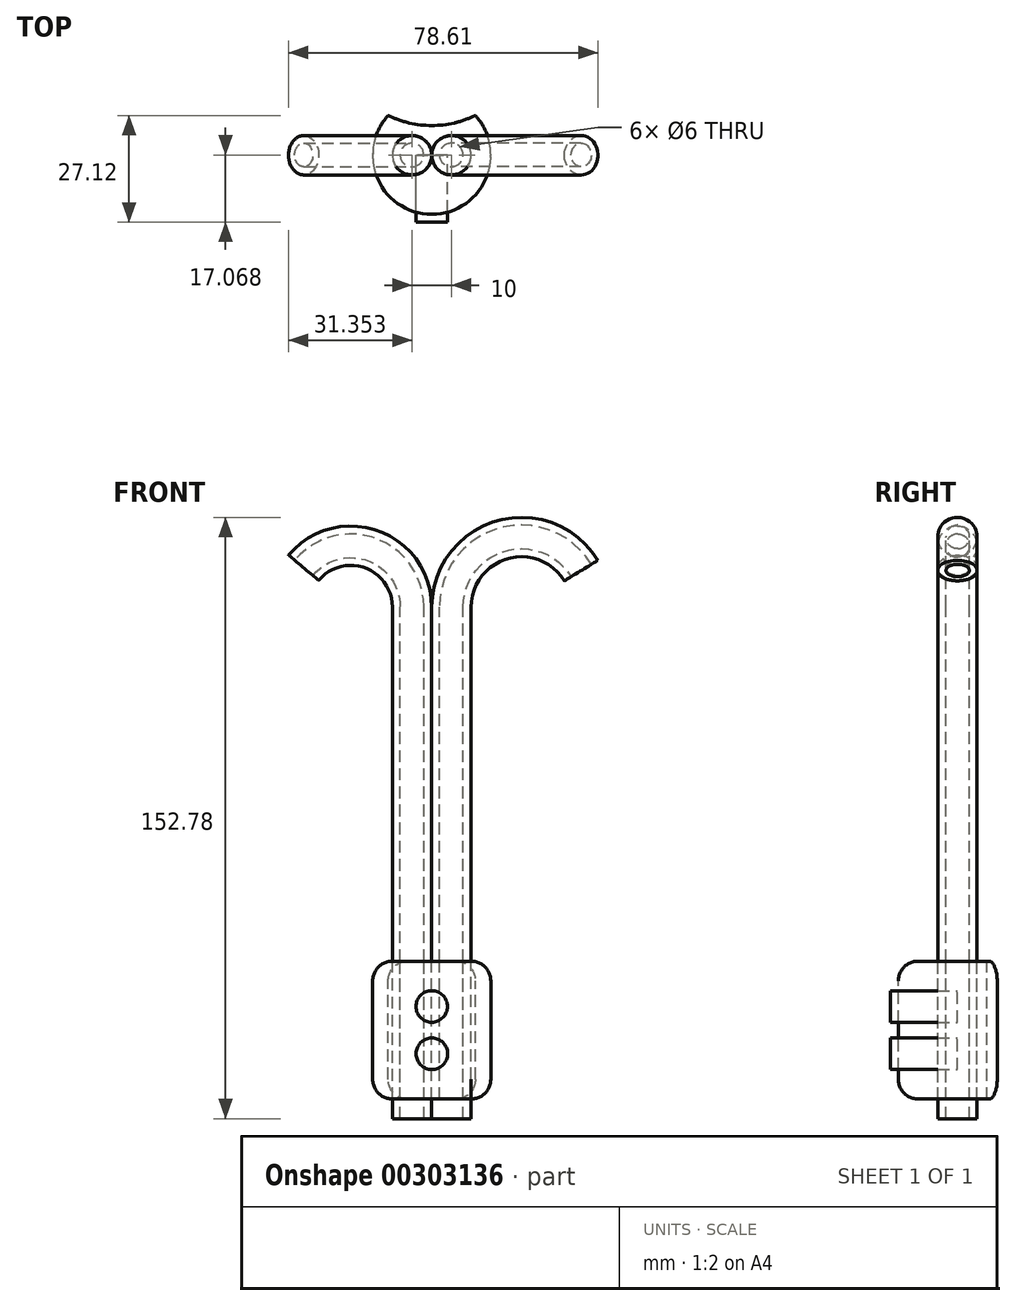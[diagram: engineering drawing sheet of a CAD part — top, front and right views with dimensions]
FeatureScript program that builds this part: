
annotation { "Feature Type Name" : "Feature", "Feature Type Description" : "" }
export const myFeature = defineFeature(function(context is Context, id is Id, definition is map)
    precondition{}
    {
        {
            var Q0;
            Q0=qCreatedBy(makeId("Top.planeOp"),FACE);
            var sketch = newSketch(context, id + "F0", { "sketchPlane" : qUnion([Q0])});
            skCircle(sketch, "E0", {"center": v(0, 0) * mm, "radius": 15 * mm});
            skCircle(sketch, "E1", {"center": v(0, 32.54) * mm, "radius": 25 * mm});
            skCircle(sketch, "E2", {"center": v(-5, 0) * mm, "radius": 5 * mm});
            skCircle(sketch, "E3.1.0.0", {"center": v(5, 0) * mm, "radius": 5 * mm});
            skLineSegment(sketch, "E3.direction1", {"start": v(-5, 0) * mm, "end": v(5, 0) * mm, "construction": true});
            skCircle(sketch, "E4", {"center": v(-5.03, 0.07) * mm, "radius": 3 * mm});
            skCircle(sketch, "E5.1.0.0", {"center": v(4.97, 0.07) * mm, "radius": 3 * mm});
            skLineSegment(sketch, "E5.direction1", {"start": v(-5.03, 0.07) * mm, "end": v(4.97, 0.07) * mm, "construction": true});
            skSolve(sketch);
        }
        {
            var Q0;
            Q0=qCreatedBy(makeId("Front.planeOp"),FACE);
            var sketch = newSketch(context, id + "F1", { "sketchPlane" : qUnion([Q0])});
            skLineSegment(sketch, "E6", {"start": v(-5, 0) * mm, "end": v(-5, 90) * mm});
            skLineSegment(sketch, "E7", {"start": v(5, 0) * mm, "end": v(5, 90) * mm});
            skArc(sketch, "E8", {"start": v(-5, 90) * mm, "mid": v(-15.27, 104.64) * mm, "end": v(-32.54, 99.97) * mm});
            skArc(sketch, "E9", {"start": v(37.96, 99.26) * mm, "mid": v(17.97, 107.12) * mm, "end": v(5, 90) * mm});
            skCircle(sketch, "E10", {"center": v(0, -11.5) * mm, "radius": 4 * mm});
            skCircle(sketch, "E11.0.1.0", {"center": v(0.03, -23.5) * mm, "radius": 4 * mm});
            skLineSegment(sketch, "E11.direction1", {"start": v(0, -11.5) * mm, "end": v(2.66, -11.5) * mm, "construction": true});
            skLineSegment(sketch, "E11.direction2", {"start": v(0, -11.5) * mm, "end": v(0.03, -23.5) * mm, "construction": true});
            skSolve(sketch);
        }
        {
            var Q0;
            Q0=makeQuery(id+"F0.imprint","IMPRINT",FACE,{"disambiguationData":[TD([[makeQuery(id+"F0.imprint","IMPRINT",EDGE,{"derivedFrom":sQuery(id+"F0.wireOp",EDGE,"E2")}),1.0]])]});
            var Q1;
            Q1=sQuery(id+"F1.wireOp",EDGE,"E6");
            var Q2;
            Q2=sQuery(id+"F1.wireOp",EDGE,"E8");
            sweep(context, id + "F2", {"profiles" : qUnion([Q0]), "path" : qUnion([Q1, Q2])});
        }
        {
            var Q0;
            Q0=makeQuery(id+"F0.imprint","IMPRINT",FACE,{"disambiguationData":[TD([[makeQuery(id+"F0.imprint","IMPRINT",EDGE,{"derivedFrom":sQuery(id+"F0.wireOp",EDGE,"E3.1.0.0")}),1.0]])]});
            var Q1;
            Q1=sQuery(id+"F1.wireOp",EDGE,"E7");
            var Q2;
            Q2=sQuery(id+"F1.wireOp",EDGE,"E9");
            sweep(context, id + "F3", {"operationType" : NewBodyOperationType.ADD, "profiles" : qUnion([Q0]), "path" : qUnion([Q1, Q2])});
        }
        {
            var Q0;
            Q0=makeQuery(id+"F0.imprint","IMPRINT",FACE,{"disambiguationData":[TD([[makeQuery(id+"F0.imprint","IMPRINT",EDGE,{"derivedFrom":sQuery(id+"F0.wireOp",EDGE,"E2")}),-1.0]])]});
            var Q1;
            Q1=makeQuery(id+"F0.imprint","IMPRINT",FACE,{"disambiguationData":[TD([[makeQuery(id+"F0.imprint","IMPRINT",EDGE,{"derivedFrom":sQuery(id+"F0.wireOp",EDGE,"E2")}),1.0]])]});
            var Q2;
            Q2=makeQuery(id+"F0.imprint","IMPRINT",FACE,{"disambiguationData":[TD([[makeQuery(id+"F0.imprint","IMPRINT",EDGE,{"derivedFrom":sQuery(id+"F0.wireOp",EDGE,"E3.1.0.0")}),1.0]])]});
            extrude(context, id + "F4", {"entities" : qUnion([Q0, Q1, Q2]), "oppositeDirection" : true, "depth" : 35 * mm});
        }
        {
            var Q0;
            Q0=makeQuery(id+"F1.imprint","IMPRINT",FACE,{"disambiguationData":[TD([[makeQuery(id+"F1.imprint","IMPRINT",EDGE,{"derivedFrom":sQuery(id+"F1.wireOp",EDGE,"E10")}),1.0]])]});
            var Q1;
            Q1=makeQuery(id+"F1.imprint","IMPRINT",FACE,{"disambiguationData":[TD([[makeQuery(id+"F1.imprint","IMPRINT",EDGE,{"derivedFrom":sQuery(id+"F1.wireOp",EDGE,"E11.0.1.0")}),1.0]])]});
            extrude(context, id + "F5", {"entities" : qUnion([Q0, Q1]), "depth" : 17 * mm});
        }
        {
            var Q0;
            Q0=makeQuery(id+"F4.opExtrude","CAP_EDGE",EDGE,{"disambiguationData":[OSD([sQuery(id+"F0.wireOp",EDGE,"E0")])],"isStart":false});
            var Q1;
            Q1=makeQuery(id+"F4.opExtrude","CAP_EDGE",EDGE,{"disambiguationData":[OSD([sQuery(id+"F0.wireOp",EDGE,"E0")])],"isStart":true});
            fillet(context, id + "F6", {"entities" : qUnion([Q0, Q1]), "radius" : 5 * mm, "tangentPropagation" : true, "allowEdgeOverflow" : false});
        }
        {
            var Q0;
            Q0=makeQuery(id+"F0.imprint","IMPRINT",FACE,{"disambiguationData":[TD([[makeQuery(id+"F0.imprint","IMPRINT",EDGE,{"derivedFrom":sQuery(id+"F0.wireOp",EDGE,"E2")}),1.0]])]});
            var Q1;
            Q1=makeQuery(id+"F0.imprint","IMPRINT",FACE,{"disambiguationData":[TD([[makeQuery(id+"F0.imprint","IMPRINT",EDGE,{"derivedFrom":sQuery(id+"F0.wireOp",EDGE,"E3.1.0.0")}),1.0]])]});
            extrude(context, id + "F7", {"entities" : qUnion([Q0, Q1]), "oppositeDirection" : true, "depth" : 40 * mm});
        }
    });
